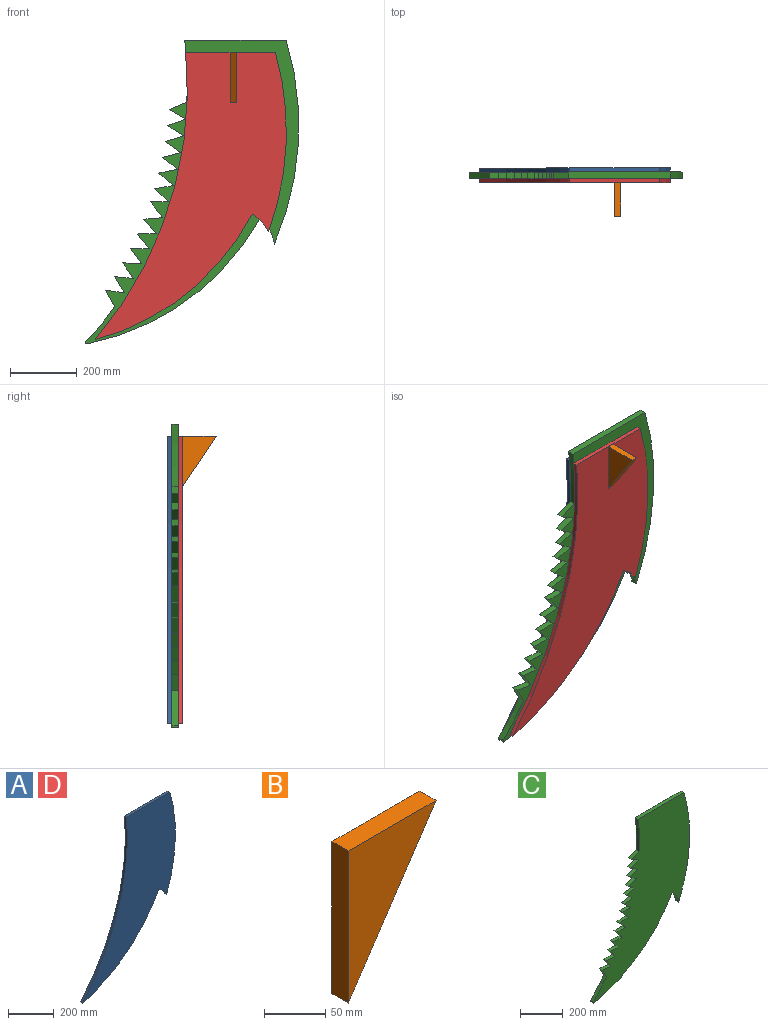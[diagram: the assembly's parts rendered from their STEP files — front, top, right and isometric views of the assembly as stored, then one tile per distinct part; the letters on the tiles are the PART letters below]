
ASSEMBLY  parts=4 mates=3
PART A: 7 faces, bbox 575x12.7x864 mm
  f0: plane 269.4x12.7mm, normal (0,0,1), area 3421.3mm2, adj f1,f4,f5,f6
  f1: cylinder r=1162.05mm len=864.04mm, axis (0,1,0), area 11818.5mm2, adj f0,f2,f5,f6
  f2: cylinder r=742.95mm len=471.6mm, axis (0,1,0), area 7897.3mm2, adj f1,f3,f5,f6
  f3: cylinder r=147.29mm len=52.33mm, axis (0,1,0), area 926.7mm2, adj f2,f4,f5,f6
  f4: cylinder r=869.95mm len=539.26mm, axis (0,1,0), area 6968.4mm2, adj f0,f3,f5,f6
  f5: plane 864.04x575.01mm, normal (0,-1,0), area 217314.6mm2, adj f0,f1,f2,f3,f4
  f6: plane 864.04x575.01mm, normal (0,1,0), area 217314.6mm2, adj f0,f1,f2,f3,f4
PART B: 5 faces, bbox 101.6x19.1x152.4 mm
  f0: plane 101.6x19.05mm, normal (0,0,1), area 1935.5mm2, adj f1,f2,f3,f4
  f1: plane 152.4x19.05mm, normal (-1,0,0), area 2903.2mm2, adj f0,f2,f3,f4
  f2: plane 152.4x101.6mm, normal (0.83,0,-0.55), area 3489.2mm2, adj f0,f1,f3,f4
  f3: plane 152.4x101.6mm, normal (0,-1,0), area 7741.9mm2, adj f0,f1,f2
  f4: plane 152.4x101.6mm, normal (0,1,0), area 7741.9mm2, adj f0,f1,f2
PART C: 35 faces, bbox 640.8x19.1x912.3 mm
  f0: plane 44.19x35.68mm, normal (-0.78,0,-0.63), area 1082mm2, adj f1,f32,f33,f34
  f1: plane 56.79x19.05mm, normal (0.01,0,1), area 1082mm2, adj f0,f2,f33,f34
  f2: plane 45.73x33.69mm, normal (-0.81,0,-0.59), area 1082mm2, adj f1,f3,f33,f34
  f3: plane 56.72x19.05mm, normal (0.05,0,1), area 1082mm2, adj f2,f4,f33,f34
  f4: plane 47.18x31.62mm, normal (-0.83,0,-0.56), area 1082mm2, adj f3,f5,f33,f34
  f5: plane 56.53x19.05mm, normal (0.1,0,1), area 1082mm2, adj f4,f6,f33,f34
  f6: plane 48.54x29.49mm, normal (-0.85,0,-0.52), area 1082mm2, adj f5,f7,f33,f34
  f7: plane 56.23x19.05mm, normal (0.14,0,0.99), area 1082mm2, adj f6,f8,f33,f34
  f8: plane 49.8x27.31mm, normal (-0.88,0,-0.48), area 1082mm2, adj f7,f9,f33,f34
  f9: cylinder r=832.68mm len=105.11mm, axis (0,1,0), area 2593.4mm2, adj f8,f10,f33,f34
  f10: cylinder r=3.81mm len=19.05mm, axis (0,1,0), area 182.2mm2, adj f9,f11,f33,f34
  f11: cylinder r=762mm len=520.18mm, axis (0,1,0), area 12643mm2, adj f10,f12,f33,f34
  f12: cylinder r=128.24mm len=78.3mm, axis (0,1,0), area 1729.4mm2, adj f11,f13,f33,f34
  f13: cylinder r=889mm len=612.76mm, axis (0,1,0), area 11938.7mm2, adj f12,f14,f33,f34
  f14: plane 304.8x19.05mm, normal (0,0,1), area 5806.4mm2, adj f13,f15,f33,f34
  f15: cylinder r=899.29mm len=186.56mm, axis (0,1,0), area 3562.3mm2, adj f14,f16,f33,f34
  f16: plane 52.5x21.67mm, normal (-0.38,0,0.92), area 1082mm2, adj f15,f17,f33,f34
  f17: plane 48.84x29mm, normal (-0.51,0,-0.86), area 1082mm2, adj f16,f18,f33,f34
  f18: plane 53.41x19.31mm, normal (-0.34,0,0.94), area 1082mm2, adj f17,f19,f33,f34
  f19: plane 47.5x31.14mm, normal (-0.55,0,-0.84), area 1082mm2, adj f18,f20,f33,f34
  f20: plane 54.22x19.05mm, normal (-0.3,0,0.95), area 1082mm2, adj f19,f21,f33,f34
  f21: plane 46.07x33.22mm, normal (-0.58,0,-0.81), area 1082mm2, adj f20,f22,f33,f34
  f22: plane 54.92x19.05mm, normal (-0.26,0,0.97), area 1082mm2, adj f21,f23,f33,f34
  f23: plane 44.55x35.23mm, normal (-0.62,0,-0.78), area 1082mm2, adj f22,f24,f33,f34
  f24: plane 55.51x19.05mm, normal (-0.21,0,0.98), area 1082mm2, adj f23,f25,f33,f34
  f25: plane 42.94x37.18mm, normal (-0.65,0,-0.76), area 1082mm2, adj f24,f26,f33,f34
  f26: plane 55.99x19.05mm, normal (-0.17,0,0.99), area 1082mm2, adj f25,f27,f33,f34
  f27: plane 41.24x39.05mm, normal (-0.69,0,-0.73), area 1082mm2, adj f26,f28,f33,f34
  f28: plane 53.86x19.05mm, normal (0,0,1), area 1026.1mm2, adj f27,f29,f33,f34
  f29: plane 47.91x36.98mm, normal (-0.79,0,-0.61), area 1152.9mm2, adj f28,f30,f33,f34
  f30: plane 56.61x19.05mm, normal (-0.08,0,1), area 1082mm2, adj f29,f31,f33,f34
  f31: plane 42.56x37.61mm, normal (-0.75,0,-0.66), area 1082mm2, adj f30,f32,f33,f34
  f32: plane 56.76x19.05mm, normal (-0.04,0,1), area 1082mm2, adj f0,f31,f33,f34
  f33: plane 912.33x640.83mm, normal (0,-1,0), area 282853.9mm2, adj f0,f1,f2,f3,f4,f5,f6,f7
  f34: plane 912.33x640.83mm, normal (0,1,0), area 282853.9mm2, adj f0,f1,f2,f3,f4,f5,f6,f7
PART D: same geometry as A
PLACE A t=(31.22,6.35,-28.45)mm
PLACE B rot(axis=(0,0,-1),90deg) t=(206.11,-38.1,-47.5)mm
PLACE C t=(49.61,-6.35,-11.92)mm
PLACE D t=(31.22,-25.4,-28.45)mm
MATE fastened B.f1 <-> D.f5  axis (0,1,0) through (187.06,-38.1,-47.5)mm
MATE fastened C.f33 <-> D.f6  axis (0,-1,0) through (140.9,-25.4,-422.28)mm
MATE fastened C.f34 <-> A.f5  axis (0,1,0) through (140.9,-6.35,-422.28)mm
